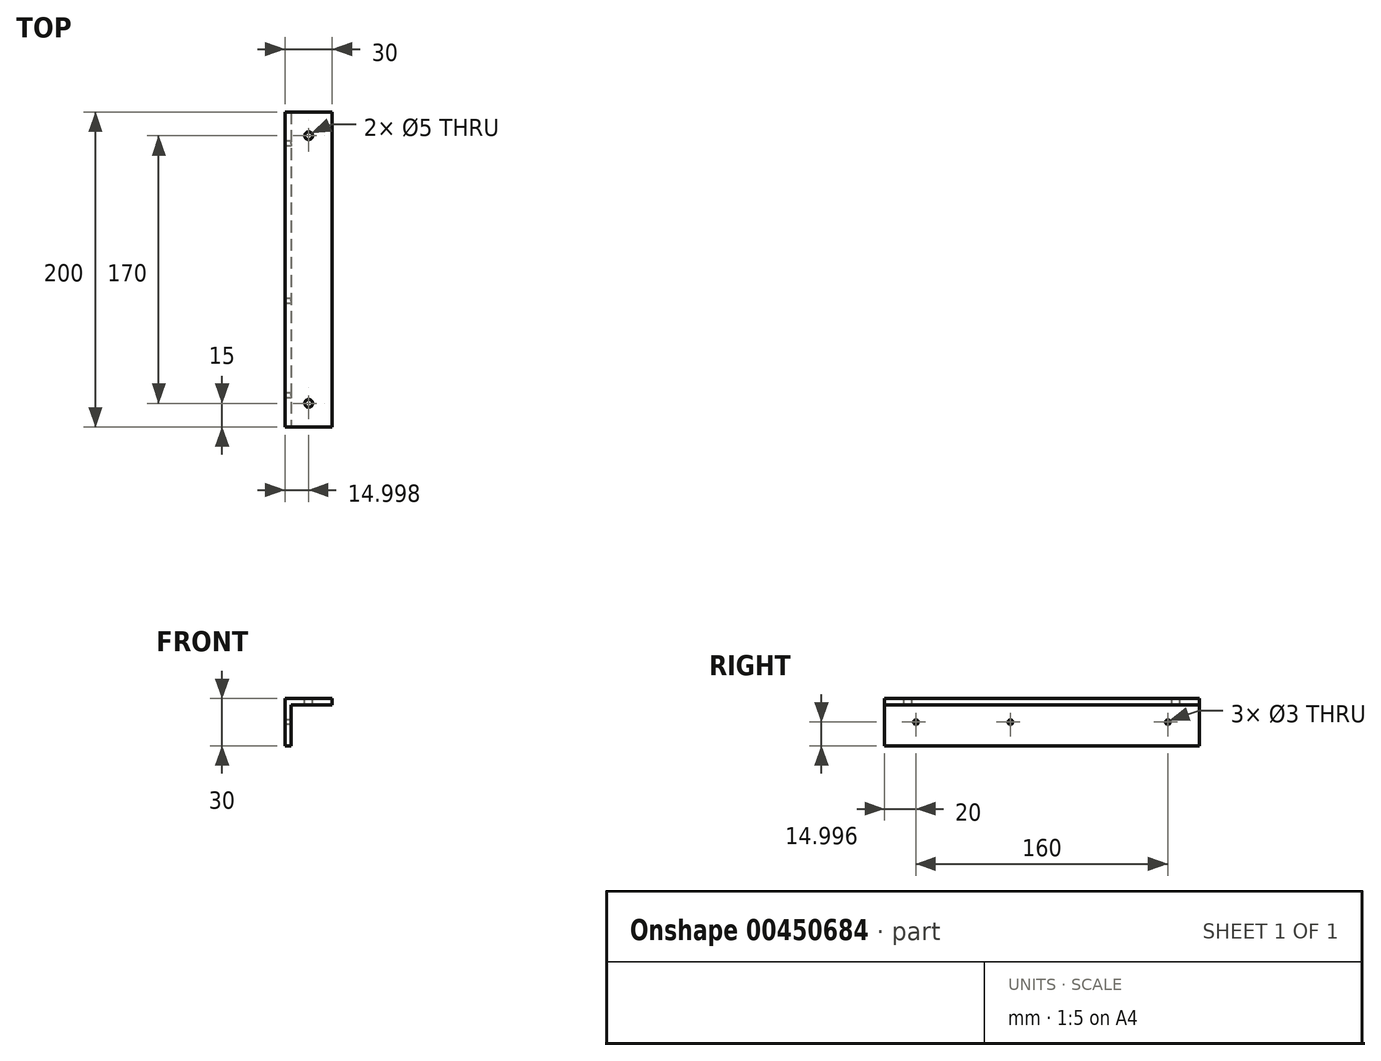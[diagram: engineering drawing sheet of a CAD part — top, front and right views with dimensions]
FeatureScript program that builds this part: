
annotation { "Feature Type Name" : "Feature", "Feature Type Description" : "" }
export const myFeature = defineFeature(function(context is Context, id is Id, definition is map)
    precondition{}
    {
        {
            var Q0;
            Q0=qCreatedBy(makeId("Front.planeOp"),FACE);
            var sketch = newSketch(context, id + "F0", { "sketchPlane" : qUnion([Q0])});
            skLineSegment(sketch, "E0", {"start": v(14.79, -34.16) * mm, "end": v(-11.21, -34.16) * mm});
            skLineSegment(sketch, "E1", {"start": v(-15.21, -60.16) * mm, "end": v(-15.21, -30.16) * mm});
            skLineSegment(sketch, "E2", {"start": v(14.79, -34.16) * mm, "end": v(14.79, -30.16) * mm});
            skLineSegment(sketch, "E3", {"start": v(-11.21, -60.16) * mm, "end": v(-11.21, -34.16) * mm});
            skLineSegment(sketch, "E4", {"start": v(-11.21, -60.16) * mm, "end": v(-15.21, -60.16) * mm});
            skLineSegment(sketch, "E5", {"start": v(-274.36, -60.16) * mm, "end": v(-74.36, -60.16) * mm});
            skLineSegment(sketch, "E6", {"start": v(-74.36, -60.16) * mm, "end": v(-74.36, -30.16) * mm});
            skLineSegment(sketch, "E7", {"start": v(-274.36, -60.16) * mm, "end": v(-274.36, -30.16) * mm});
            skLineSegment(sketch, "E8", {"start": v(-74.36, -34.25) * mm, "end": v(-274.36, -34.25) * mm});
            skLineSegment(sketch, "E9", {"start": v(-274.36, -30.16) * mm, "end": v(-74.36, -30.16) * mm});
            skLineSegment(sketch, "E10", {"start": v(14.79, -30.16) * mm, "end": v(-15.21, -30.16) * mm});
            skLineSegment(sketch, "E11", {"start": v(-74.36, 79.72) * mm, "end": v(-274.36, 79.72) * mm});
            skLineSegment(sketch, "E12", {"start": v(-74.36, 49.72) * mm, "end": v(-74.36, 79.72) * mm});
            skLineSegment(sketch, "E13", {"start": v(-274.36, 49.72) * mm, "end": v(-274.36, 79.72) * mm});
            skLineSegment(sketch, "E14", {"start": v(-274.36, 49.72) * mm, "end": v(-74.36, 49.72) * mm});
            skLineSegment(sketch, "E15", {"start": v(-274.36, 53.72) * mm, "end": v(-74.36, 53.72) * mm});
            skLineSegment(sketch, "E16", {"start": v(-94.36, -42.91) * mm, "end": v(-94.36, -47.41) * mm});
            skCircle(sketch, "E17", {"center": v(-94.36, -45.16) * mm, "radius": 1.23 * mm});
            skCircle(sketch, "E18", {"center": v(-94.36, -45.16) * mm, "radius": 1.5 * mm});
            skLineSegment(sketch, "E19", {"start": v(-92.11, -45.16) * mm, "end": v(-96.61, -45.16) * mm});
            skLineSegment(sketch, "E20", {"start": v(-254.36, -42.91) * mm, "end": v(-254.36, -47.41) * mm});
            skCircle(sketch, "E21", {"center": v(-254.36, -45.16) * mm, "radius": 1.23 * mm});
            skCircle(sketch, "E22", {"center": v(-254.36, -45.16) * mm, "radius": 1.5 * mm});
            skLineSegment(sketch, "E23", {"start": v(-252.11, -45.16) * mm, "end": v(-256.61, -45.16) * mm});
            skLineSegment(sketch, "E24", {"start": v(-89.36, 60.97) * mm, "end": v(-89.36, 68.47) * mm});
            skCircle(sketch, "E25", {"center": v(-89.36, 64.72) * mm, "radius": 2.07 * mm});
            skCircle(sketch, "E26", {"center": v(-89.36, 64.72) * mm, "radius": 2.5 * mm});
            skLineSegment(sketch, "E27", {"start": v(-85.61, 64.72) * mm, "end": v(-93.11, 64.72) * mm});
            skLineSegment(sketch, "E28", {"start": v(-259.36, 60.97) * mm, "end": v(-259.36, 68.47) * mm});
            skCircle(sketch, "E29", {"center": v(-259.36, 64.72) * mm, "radius": 2.07 * mm});
            skCircle(sketch, "E30", {"center": v(-259.36, 64.72) * mm, "radius": 2.5 * mm});
            skLineSegment(sketch, "E31", {"start": v(-255.61, 64.72) * mm, "end": v(-263.11, 64.72) * mm});
            skLineSegment(sketch, "E32", {"start": v(-29.43, -27.66) * mm, "end": v(-27.99, -30.16) * mm});
            skLineSegment(sketch, "E33", {"start": v(-27.99, -30.16) * mm, "end": v(-24.81, -24.66) * mm});
            skCircle(sketch, "E34", {"center": v(-27.99, -28.5) * mm, "radius": 0.83 * mm});
            skLineSegment(sketch, "E35", {"start": v(-24.81, -24.66) * mm, "end": v(-17.59, -24.66) * mm});
            skCircle(sketch, "E36", {"center": v(-24.81, -24.66) * mm, "radius": 0.79 * mm});
            skLineSegment(sketch, "E37", {"start": v(-154.36, -42.91) * mm, "end": v(-154.36, -47.41) * mm});
            skCircle(sketch, "E38", {"center": v(-154.36, -45.16) * mm, "radius": 1.23 * mm});
            skCircle(sketch, "E39", {"center": v(-154.36, -45.16) * mm, "radius": 1.5 * mm});
            skLineSegment(sketch, "E40", {"start": v(-152.11, -45.16) * mm, "end": v(-156.61, -45.16) * mm});
            skSolve(sketch);
        }
        {
            var Q0;
            Q0=makeQuery(id+"F0.imprint","IMPRINT",FACE,{"disambiguationData":[TD([[makeQuery(id+"F0.imprint","IMPRINT",EDGE,{"derivedFrom":sQuery(id+"F0.wireOp",EDGE,"E0")}),-1.0]])]});
            extrude(context, id + "F1", {"entities" : qUnion([Q0]), "oppositeDirection" : true, "depth" : 200 * mm});
        }
        {
            var Q0;
            Q0=makeQuery(id+"F1.opExtrude","SWEPT_FACE",FACE,{"disambiguationData":[OSD([sQuery(id+"F0.wireOp",EDGE,"E10")])]});
            var sketch = newSketch(context, id + "F2", { "sketchPlane" : qUnion([Q0])});
            skSolve(sketch);
        }
        {
            var Q0;
            Q0=makeQuery(id+"F1.opExtrude","SWEPT_FACE",FACE,{"disambiguationData":[OSD([sQuery(id+"F0.wireOp",EDGE,"E1")])]});
            var sketch = newSketch(context, id + "F3", { "sketchPlane" : qUnion([Q0])});
            skLineSegment(sketch, "E41", {"start": v(-274.36, -60.16) * mm, "end": v(-74.36, -60.16) * mm});
            skLineSegment(sketch, "E42", {"start": v(0, -60.16) * mm, "end": v(0, -30.16) * mm});
            skLineSegment(sketch, "E43", {"start": v(-200, -60.16) * mm, "end": v(-200, -30.16) * mm});
            skLineSegment(sketch, "E44", {"start": v(-74.36, -34.25) * mm, "end": v(-274.36, -34.25) * mm});
            skLineSegment(sketch, "E45", {"start": v(-274.36, -30.16) * mm, "end": v(-74.36, -30.16) * mm});
            skLineSegment(sketch, "E46", {"start": v(-74.36, 79.72) * mm, "end": v(-274.36, 79.72) * mm});
            skLineSegment(sketch, "E47", {"start": v(-74.36, 49.72) * mm, "end": v(-74.36, 79.72) * mm});
            skLineSegment(sketch, "E48", {"start": v(-274.36, 49.72) * mm, "end": v(-274.36, 79.72) * mm});
            skLineSegment(sketch, "E49", {"start": v(-274.36, 49.72) * mm, "end": v(-74.36, 49.72) * mm});
            skLineSegment(sketch, "E50", {"start": v(-274.36, 53.72) * mm, "end": v(-74.36, 53.72) * mm});
            skLineSegment(sketch, "E51", {"start": v(-20, -42.91) * mm, "end": v(-20, -47.41) * mm});
            skCircle(sketch, "E52", {"center": v(-94.36, -45.16) * mm, "radius": 1.23 * mm});
            skCircle(sketch, "E53", {"center": v(-20, -45.16) * mm, "radius": 1.5 * mm});
            skLineSegment(sketch, "E54", {"start": v(-17.75, -45.16) * mm, "end": v(-22.25, -45.16) * mm});
            skLineSegment(sketch, "E55", {"start": v(-180, -42.91) * mm, "end": v(-180, -47.41) * mm});
            skCircle(sketch, "E56", {"center": v(-254.36, -45.16) * mm, "radius": 1.23 * mm});
            skCircle(sketch, "E57", {"center": v(-180, -45.16) * mm, "radius": 1.5 * mm});
            skLineSegment(sketch, "E58", {"start": v(-177.75, -45.16) * mm, "end": v(-182.25, -45.16) * mm});
            skLineSegment(sketch, "E59", {"start": v(-89.36, 60.97) * mm, "end": v(-89.36, 68.47) * mm});
            skCircle(sketch, "E60", {"center": v(-89.36, 64.72) * mm, "radius": 2.07 * mm});
            skCircle(sketch, "E61", {"center": v(-89.36, 64.72) * mm, "radius": 2.5 * mm});
            skLineSegment(sketch, "E62", {"start": v(-85.61, 64.72) * mm, "end": v(-93.11, 64.72) * mm});
            skLineSegment(sketch, "E63", {"start": v(-259.36, 60.97) * mm, "end": v(-259.36, 68.47) * mm});
            skCircle(sketch, "E64", {"center": v(-259.36, 64.72) * mm, "radius": 2.07 * mm});
            skCircle(sketch, "E65", {"center": v(-259.36, 64.72) * mm, "radius": 2.5 * mm});
            skLineSegment(sketch, "E66", {"start": v(-255.61, 64.72) * mm, "end": v(-263.11, 64.72) * mm});
            skLineSegment(sketch, "E67", {"start": v(-80, -42.91) * mm, "end": v(-80, -47.41) * mm});
            skCircle(sketch, "E68", {"center": v(-154.36, -45.16) * mm, "radius": 1.23 * mm});
            skCircle(sketch, "E69", {"center": v(-80, -45.16) * mm, "radius": 1.5 * mm});
            skLineSegment(sketch, "E70", {"start": v(-77.75, -45.16) * mm, "end": v(-82.25, -45.16) * mm});
            skSolve(sketch);
        }
        {
            var Q0;
            Q0=sQuery(id+"F3.wireOp",VERTEX,"E53.center");
            var Q1;
            Q1=sQuery(id+"F3.wireOp",VERTEX,"E69.center");
            var Q2;
            Q2=sQuery(id+"F3.wireOp",VERTEX,"E57.center");
            var Q3;
            Q3=makeQuery(id+"F1.opExtrude","SWEPT_BODY",BODY,{"disambiguationData":[OSD([sQuery(id+"F0.wireOp",EDGE,"E0"),sQuery(id+"F0.wireOp",EDGE,"E1"),sQuery(id+"F0.wireOp",EDGE,"E2"),sQuery(id+"F0.wireOp",EDGE,"E3"),sQuery(id+"F0.wireOp",EDGE,"E4"),sQuery(id+"F0.wireOp",EDGE,"E10")])]});
            hole(context, id + "F4", {"style" : HoleStyle.SIMPLE, "endStyle" : HoleEndStyle.THROUGH, "holeDiameter" : 3 * mm, "isTappedThrough" : true, "tappedDepth" : 12 * mm, "tapClearance" : 3, "locations" : qUnion([Q0, Q1, Q2]), "scope" : qUnion([Q3])});
        }
        {
            var Q0;
            {var subQ0=sQuery(id+"F0.wireOp",EDGE,"E10");Q0=makeQuery(id+"F2.imprint","IMPRINT",FACE,{"disambiguationData":[TD([[makeQuery(id+"F2.imprint","IMPRINT",EDGE,{"derivedFrom":makeQuery(id+"F1.opExtrude","CAP_EDGE",EDGE,{"disambiguationData":[OSD([subQ0])],"isStart":true})}),-1.0]])]});}
            var sketch = newSketch(context, id + "F5", { "sketchPlane" : qUnion([Q0])});
            skLineSegment(sketch, "E71.0", {"start": v(-0.21, 15) * mm, "end": v(-0.21, 15) * mm});
            skLineSegment(sketch, "E71.2", {"start": v(-0.21, 185) * mm, "end": v(-0.21, 185) * mm});
            skCircle(sketch, "E72", {"center": v(-0.21, 15) * mm, "radius": 2.5 * mm});
            skCircle(sketch, "E73", {"center": v(-0.21, 185) * mm, "radius": 2.5 * mm});
            skSolve(sketch);
        }
        {
            var Q0;
            Q0=sQuery(id+"F5.wireOp",VERTEX,"E73.center");
            var Q1;
            Q1=sQuery(id+"F5.wireOp",VERTEX,"E72.center");
            var Q2;
            Q2=makeQuery(id+"F1.opExtrude","SWEPT_BODY",BODY,{"disambiguationData":[OSD([sQuery(id+"F0.wireOp",EDGE,"E0"),sQuery(id+"F0.wireOp",EDGE,"E1"),sQuery(id+"F0.wireOp",EDGE,"E2"),sQuery(id+"F0.wireOp",EDGE,"E3"),sQuery(id+"F0.wireOp",EDGE,"E4"),sQuery(id+"F0.wireOp",EDGE,"E10")])]});
            hole(context, id + "F6", {"style" : HoleStyle.SIMPLE, "endStyle" : HoleEndStyle.THROUGH, "holeDiameter" : 5 * mm, "isTappedThrough" : true, "tappedDepth" : 12 * mm, "tapClearance" : 3, "locations" : qUnion([Q0, Q1]), "scope" : qUnion([Q2])});
        }
    });
